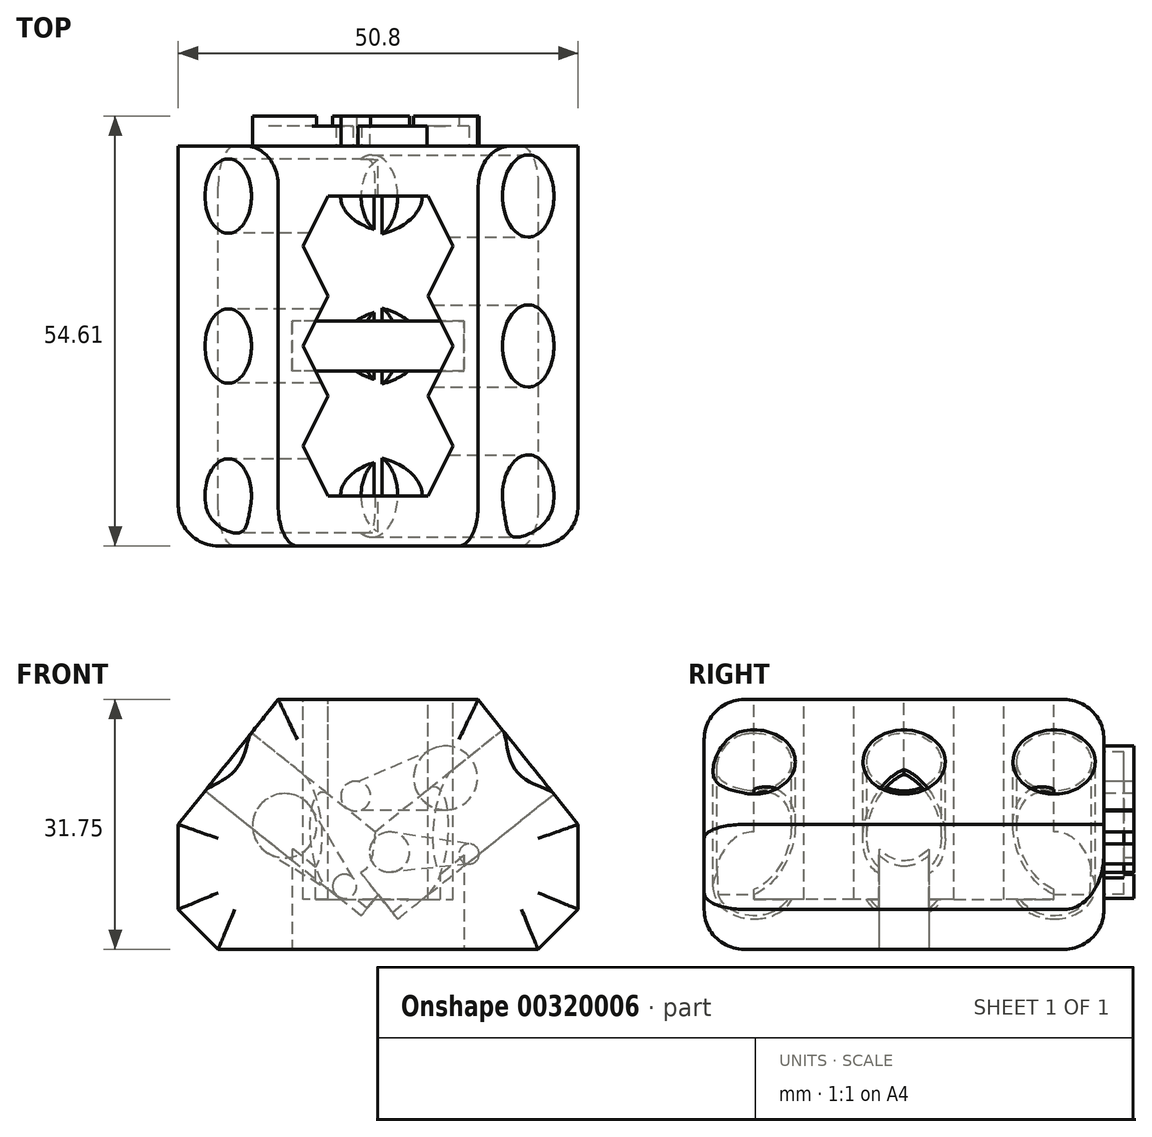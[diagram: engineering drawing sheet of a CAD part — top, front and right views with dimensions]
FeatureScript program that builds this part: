
annotation { "Feature Type Name" : "Feature", "Feature Type Description" : "" }
export const myFeature = defineFeature(function(context is Context, id is Id, definition is map)
    precondition{}
    {
        {
            var Q0;
            Q0=qCreatedBy(makeId("Top.planeOp"),FACE);
            var sketch = newSketch(context, id + "F0", { "sketchPlane" : qUnion([Q0])});
            skLineSegment(sketch, "E0.bottom", {"start": v(-25.4, 30.27) * mm, "end": v(25.4, 30.27) * mm});
            skLineSegment(sketch, "E0.top", {"start": v(-25.4, -20.53) * mm, "end": v(25.4, -20.53) * mm});
            skLineSegment(sketch, "E0.left", {"start": v(-25.4, 30.27) * mm, "end": v(-25.4, -20.53) * mm});
            skLineSegment(sketch, "E0.right", {"start": v(25.4, 30.27) * mm, "end": v(25.4, -20.53) * mm});
            skSolve(sketch);
        }
        {
            var Q0;
            Q0=makeQuery(id+"F0.imprint","IMPRINT",FACE,{"disambiguationData":[TD([[makeQuery(id+"F0.imprint","IMPRINT",EDGE,{"derivedFrom":sQuery(id+"F0.wireOp",EDGE,"E0.bottom")}),-1.0]])]});
            extrude(context, id + "F1", {"entities" : qUnion([Q0]), "depth" : 31.75 * mm});
        }
        {
            var Q0;
            Q0=makeQuery(id+"F1.opExtrude","SWEPT_FACE",FACE,{"disambiguationData":[OSD([sQuery(id+"F0.wireOp",EDGE,"E0.top")])]});
            var sketch = newSketch(context, id + "F2", { "sketchPlane" : qUnion([Q0])});
            skLineSegment(sketch, "E1", {"start": v(0, 31.75) * mm, "end": v(0, 0) * mm, "construction": true});
            skLineSegment(sketch, "E2", {"start": v(0, 0) * mm, "end": v(-25.4, 15.88) * mm, "construction": true});
            skLineSegment(sketch, "E3", {"start": v(-25.4, 15.88) * mm, "end": v(0, 31.75) * mm, "construction": true});
            skLineSegment(sketch, "E4", {"start": v(0, 0) * mm, "end": v(25.4, 15.88) * mm, "construction": true});
            skLineSegment(sketch, "E5", {"start": v(25.4, 15.87) * mm, "end": v(0, 31.75) * mm, "construction": true});
            skLineSegment(sketch, "E6", {"start": v(-12.7, 23.81) * mm, "end": v(-12.7, 31.75) * mm, "construction": true});
            skPoint(sketch, "E6.endSnap0", {"position": v(-12.7, 23.81) * mm});
            skLineSegment(sketch, "E7", {"start": v(12.7, 23.81) * mm, "end": v(12.7, 31.75) * mm, "construction": true});
            skPoint(sketch, "E7.endSnap0", {"position": v(12.7, 23.81) * mm});
            skLineSegment(sketch, "E8", {"start": v(-12.7, 31.75) * mm, "end": v(-25.4, 15.88) * mm});
            skLineSegment(sketch, "E9", {"start": v(12.7, 31.75) * mm, "end": v(25.4, 15.87) * mm});
            skSolve(sketch);
        }
        {
            var Q0;
            {var subQ0=sQuery(id+"F2.wireOp",EDGE,"E8");Q0=makeQuery(id+"F2.imprint","IMPRINT",FACE,{"disambiguationData":[TD([[makeQuery(id+"F2.imprint","IMPRINT",EDGE,{"derivedFrom":subQ0}),-1.0]])]});}
            var Q1;
            {var subQ0=sQuery(id+"F2.wireOp",EDGE,"E9");Q1=makeQuery(id+"F2.imprint","IMPRINT",FACE,{"disambiguationData":[TD([[makeQuery(id+"F2.imprint","IMPRINT",EDGE,{"derivedFrom":subQ0}),1.0]])]});}
            extrude(context, id + "F3", {"entities" : qUnion([Q0, Q1]), "operationType" : NewBodyOperationType.REMOVE, "oppositeDirection" : true, "depth" : 50.8 * mm});
        }
        {
            var Q0;
            Q0=makeQuery(id+"F3.boolean.opBoolean","COPY",FACE,{"derivedFrom":makeQuery(id+"F3.opExtrude","SWEPT_FACE",FACE,{"disambiguationData":[OSD([sQuery(id+"F2.wireOp",EDGE,"E8")])]})});
            var sketch = newSketch(context, id + "F4", { "sketchPlane" : qUnion([Q0])});
            skLineSegment(sketch, "E10", {"start": v(-30.27, 16.86) * mm, "end": v(-4.87, 16.86) * mm, "construction": true});
            skLineSegment(sketch, "E11", {"start": v(-4.87, 16.86) * mm, "end": v(-4.87, -3.47) * mm, "construction": true});
            skLineSegment(sketch, "E12", {"start": v(-4.87, 6.7) * mm, "end": v(20.53, 6.7) * mm, "construction": true});
            skLineSegment(sketch, "E13", {"start": v(20.53, 6.7) * mm, "end": v(7.83, 6.7) * mm, "construction": true});
            skLineSegment(sketch, "E14", {"start": v(-30.27, 6.7) * mm, "end": v(-4.87, 6.7) * mm, "construction": true});
            skLineSegment(sketch, "E15", {"start": v(-17.57, 6.7) * mm, "end": v(-4.87, 6.7) * mm, "construction": true});
            skLineSegment(sketch, "E16", {"start": v(-17.57, 6.7) * mm, "end": v(-17.57, 16.86) * mm, "construction": true});
            skLineSegment(sketch, "E17", {"start": v(-17.57, 16.86) * mm, "end": v(7.83, 16.86) * mm, "construction": true});
            skLineSegment(sketch, "E18", {"start": v(7.83, 16.86) * mm, "end": v(7.83, 6.7) * mm, "construction": true});
            skLineSegment(sketch, "E19", {"start": v(14.18, 6.7) * mm, "end": v(7.83, 6.7) * mm, "construction": true});
            skLineSegment(sketch, "E20", {"start": v(-30.27, 6.7) * mm, "end": v(-17.57, 6.7) * mm, "construction": true});
            skLineSegment(sketch, "E21", {"start": v(-17.57, -3.47) * mm, "end": v(-17.57, 6.7) * mm, "construction": true});
            skLineSegment(sketch, "E22", {"start": v(-23.92, 6.7) * mm, "end": v(-17.57, 6.7) * mm, "construction": true});
            skCircle(sketch, "E23", {"center": v(-23.92, 6.7) * mm, "radius": 4.72 * mm});
            skLineSegment(sketch, "E24", {"start": v(-23.92, 11.42) * mm, "end": v(20.53, 11.42) * mm, "construction": true});
            skLineSegment(sketch, "E25", {"start": v(-4.87, 11.42) * mm, "end": v(7.83, 11.42) * mm, "construction": true});
            skLineSegment(sketch, "E26", {"start": v(7.83, 11.42) * mm, "end": v(14.18, 11.42) * mm, "construction": true});
            skCircle(sketch, "E27", {"center": v(-4.87, 6.7) * mm, "radius": 4.72 * mm});
            skCircle(sketch, "E28", {"center": v(14.18, 6.7) * mm, "radius": 4.72 * mm});
            skSolve(sketch);
        }
        {
            var Q0;
            Q0 = qSketchRegion(id + "F4", true);
            extrude(context, id + "F5", {"entities" : qUnion([Q0]), "operationType" : NewBodyOperationType.REMOVE, "oppositeDirection" : true, "depth" : 25.4 * mm});
        }
        {
            var Q0;
            Q0=makeQuery(id+"F3.boolean.opBoolean","COPY",FACE,{"derivedFrom":makeQuery(id+"F3.opExtrude","SWEPT_FACE",FACE,{"disambiguationData":[OSD([sQuery(id+"F2.wireOp",EDGE,"E9")])]})});
            var sketch = newSketch(context, id + "F6", { "sketchPlane" : qUnion([Q0])});
            skLineSegment(sketch, "E29", {"start": v(-20.53, 16.86) * mm, "end": v(4.87, 16.86) * mm, "construction": true});
            skLineSegment(sketch, "E30", {"start": v(4.87, 16.86) * mm, "end": v(4.87, -3.47) * mm, "construction": true});
            skLineSegment(sketch, "E31", {"start": v(4.87, -3.47) * mm, "end": v(30.27, -3.47) * mm, "construction": true});
            skLineSegment(sketch, "E32", {"start": v(30.27, -3.47) * mm, "end": v(30.27, 16.86) * mm, "construction": true});
            skLineSegment(sketch, "E33", {"start": v(30.27, 16.86) * mm, "end": v(4.87, 16.86) * mm, "construction": true});
            skLineSegment(sketch, "E34", {"start": v(4.87, 6.7) * mm, "end": v(30.27, 6.7) * mm, "construction": true});
            skLineSegment(sketch, "E35", {"start": v(30.27, 6.7) * mm, "end": v(17.57, 6.7) * mm, "construction": true});
            skLineSegment(sketch, "E36", {"start": v(17.57, 6.7) * mm, "end": v(23.92, 6.7) * mm, "construction": true});
            skLineSegment(sketch, "E37", {"start": v(-20.53, 6.7) * mm, "end": v(4.87, 6.7) * mm, "construction": true});
            skLineSegment(sketch, "E38", {"start": v(-7.83, 6.7) * mm, "end": v(4.87, 6.7) * mm, "construction": true});
            skLineSegment(sketch, "E39", {"start": v(-20.53, -3.47) * mm, "end": v(4.87, -3.47) * mm, "construction": true});
            skLineSegment(sketch, "E40", {"start": v(-20.53, -3.47) * mm, "end": v(-20.53, 16.86) * mm, "construction": true});
            skLineSegment(sketch, "E41", {"start": v(-20.53, 6.7) * mm, "end": v(-7.83, 6.7) * mm, "construction": true});
            skLineSegment(sketch, "E42", {"start": v(-14.18, 6.7) * mm, "end": v(-7.83, 6.7) * mm, "construction": true});
            skLineSegment(sketch, "E43", {"start": v(4.87, 11.92) * mm, "end": v(30.27, 11.92) * mm, "construction": true});
            skLineSegment(sketch, "E44", {"start": v(30.27, 11.92) * mm, "end": v(23.92, 11.92) * mm, "construction": true});
            skLineSegment(sketch, "E45", {"start": v(23.92, 11.92) * mm, "end": v(-14.18, 11.92) * mm, "construction": true});
            skCircle(sketch, "E46", {"center": v(-14.18, 6.7) * mm, "radius": 5.23 * mm});
            skCircle(sketch, "E47", {"center": v(4.87, 6.7) * mm, "radius": 5.23 * mm});
            skCircle(sketch, "E48", {"center": v(23.92, 6.7) * mm, "radius": 5.23 * mm});
            skSolve(sketch);
        }
        {
            var Q0;
            Q0=makeQuery(id+"F6.imprint","IMPRINT",FACE,{"disambiguationData":[TD([[makeQuery(id+"F6.imprint","IMPRINT",EDGE,{"derivedFrom":sQuery(id+"F6.wireOp",EDGE,"E46")}),1.0]])]});
            var Q1;
            Q1=makeQuery(id+"F6.imprint","IMPRINT",FACE,{"disambiguationData":[TD([[makeQuery(id+"F6.imprint","IMPRINT",EDGE,{"derivedFrom":sQuery(id+"F6.wireOp",EDGE,"E47")}),1.0]])]});
            var Q2;
            Q2=makeQuery(id+"F6.imprint","IMPRINT",FACE,{"disambiguationData":[TD([[makeQuery(id+"F6.imprint","IMPRINT",EDGE,{"derivedFrom":sQuery(id+"F6.wireOp",EDGE,"E48")}),1.0]])]});
            extrude(context, id + "F7", {"entities" : qUnion([Q0, Q1, Q2]), "operationType" : NewBodyOperationType.REMOVE, "oppositeDirection" : true, "depth" : 25.4 * mm});
        }
        {
            var Q0;
            Q0=makeQuery(id+"F3.boolean.opBoolean","COPY",EDGE,{"derivedFrom":makeQuery(id+"F3.opExtrude","SWEPT_EDGE",EDGE,{"disambiguationData":[OSD([sQuery(id+"F0.wireOp",EDGE,"E0.top"),sQuery(id+"F0.wireOp",EDGE,"E0.right"),sQuery(id+"F2.wireOp",EDGE,"E9")])]})});
            var Q1;
            Q1=makeQuery(id+"F3.boolean.opBoolean","COPY",EDGE,{"derivedFrom":makeQuery(id+"F3.opExtrude","SWEPT_EDGE",EDGE,{"disambiguationData":[OSD([sQuery(id+"F0.wireOp",EDGE,"E0.top"),sQuery(id+"F0.wireOp",EDGE,"E0.left"),sQuery(id+"F2.wireOp",EDGE,"E8")])]})});
            var Q2;
            Q2=makeQuery(id+"F1.opExtrude","CAP_EDGE",EDGE,{"disambiguationData":[OSD([sQuery(id+"F0.wireOp",EDGE,"E0.left")])],"isStart":true});
            var Q3;
            Q3=makeQuery(id+"F1.opExtrude","CAP_EDGE",EDGE,{"disambiguationData":[OSD([sQuery(id+"F0.wireOp",EDGE,"E0.right")])],"isStart":true});
            chamfer(context, id + "F8", {"entities" : qUnion([Q0, Q1, Q2, Q3]), "width" : 5.08 * mm, "tangentPropagation" : true});
        }
        {
            var Q0;
            Q0=makeQuery(id+"F1.opExtrude","CAP_FACE",FACE,{"disambiguationData":[OSD([sQuery(id+"F0.wireOp",EDGE,"E0.bottom"),sQuery(id+"F0.wireOp",EDGE,"E0.top"),sQuery(id+"F0.wireOp",EDGE,"E0.left"),sQuery(id+"F0.wireOp",EDGE,"E0.right")])],"isStart":false});
            var sketch = newSketch(context, id + "F9", { "sketchPlane" : qUnion([Q0])});
            skLineSegment(sketch, "E49", {"start": v(0, 30.27) * mm, "end": v(0, -20.53) * mm, "construction": true});
            skLineSegment(sketch, "E50", {"start": v(0, -20.53) * mm, "end": v(0, 4.87) * mm, "construction": true});
            skLineSegment(sketch, "E51", {"start": v(0, 4.87) * mm, "end": v(12.7, 4.87) * mm, "construction": true});
            skLineSegment(sketch, "E52", {"start": v(12.7, 4.87) * mm, "end": v(-12.7, 4.87) * mm, "construction": true});
            skLineSegment(sketch, "E53", {"start": v(-12.7, 4.87) * mm, "end": v(-12.7, 30.27) * mm, "construction": true});
            skLineSegment(sketch, "E54", {"start": v(-12.7, 30.27) * mm, "end": v(12.7, 30.27) * mm, "construction": true});
            skLineSegment(sketch, "E55", {"start": v(12.7, 30.27) * mm, "end": v(12.7, -20.53) * mm, "construction": true});
            skLineSegment(sketch, "E56", {"start": v(12.7, -20.53) * mm, "end": v(-12.7, -20.53) * mm, "construction": true});
            skLineSegment(sketch, "E57", {"start": v(-12.7, -20.53) * mm, "end": v(-12.7, 4.87) * mm, "construction": true});
            skLineSegment(sketch, "E58", {"start": v(-12.7, -7.83) * mm, "end": v(12.7, -7.83) * mm, "construction": true});
            skLineSegment(sketch, "E59", {"start": v(-12.7, 17.57) * mm, "end": v(12.7, 17.57) * mm, "construction": true});
            skLineSegment(sketch, "E60", {"start": v(12.7, 17.57) * mm, "end": v(0, 17.57) * mm, "construction": true});
            skLineSegment(sketch, "E61", {"start": v(-12.7, 30.27) * mm, "end": v(0, 17.57) * mm, "construction": true});
            skLineSegment(sketch, "E62", {"start": v(12.7, 30.27) * mm, "end": v(0, 17.57) * mm, "construction": true});
            skLineSegment(sketch, "E63", {"start": v(0, 17.57) * mm, "end": v(-12.7, 4.87) * mm, "construction": true});
            skLineSegment(sketch, "E64", {"start": v(12.7, 4.87) * mm, "end": v(0, 17.57) * mm, "construction": true});
            skLineSegment(sketch, "E65", {"start": v(-12.7, 4.87) * mm, "end": v(0, -7.83) * mm, "construction": true});
            skLineSegment(sketch, "E66", {"start": v(0, -7.83) * mm, "end": v(12.7, 4.87) * mm, "construction": true});
            skLineSegment(sketch, "E67", {"start": v(0, -7.83) * mm, "end": v(-12.7, -20.53) * mm, "construction": true});
            skLineSegment(sketch, "E68", {"start": v(0, -7.83) * mm, "end": v(12.7, -20.53) * mm, "construction": true});
            skLineSegment(sketch, "E69", {"start": v(-6.35, 23.92) * mm, "end": v(6.35, 23.92) * mm, "construction": true});
            skLineSegment(sketch, "E70", {"start": v(-6.35, 11.22) * mm, "end": v(6.35, 11.22) * mm, "construction": true});
            skLineSegment(sketch, "E71", {"start": v(-6.35, -1.48) * mm, "end": v(6.35, -1.48) * mm, "construction": true});
            skLineSegment(sketch, "E72", {"start": v(-6.35, -14.18) * mm, "end": v(6.35, -14.18) * mm, "construction": true});
            skLineSegment(sketch, "E73", {"start": v(-12.7, 17.57) * mm, "end": v(0, 17.57) * mm, "construction": true});
            skLineSegment(sketch, "E74", {"start": v(-6.35, 23.92) * mm, "end": v(-6.35, 17.57) * mm, "construction": true});
            skLineSegment(sketch, "E75", {"start": v(-6.35, 17.57) * mm, "end": v(6.35, 17.57) * mm, "construction": true});
            skLineSegment(sketch, "E76", {"start": v(6.35, 17.57) * mm, "end": v(6.35, 23.92) * mm, "construction": true});
            skLineSegment(sketch, "E77", {"start": v(-12.7, 17.57) * mm, "end": v(-6.35, 17.57) * mm, "construction": true});
            skLineSegment(sketch, "E78", {"start": v(-9.53, 20.75) * mm, "end": v(-9.53, 17.57) * mm, "construction": true});
            skPoint(sketch, "E78.startSnap0", {"position": v(-6.35, 20.75) * mm});
            skPoint(sketch, "E78.startSnap1", {"position": v(-9.53, 17.57) * mm});
            skLineSegment(sketch, "E79", {"start": v(-9.53, 17.57) * mm, "end": v(6.35, 17.57) * mm, "construction": true});
            skLineSegment(sketch, "E80", {"start": v(-9.53, 17.57) * mm, "end": v(-9.53, -20.53) * mm, "construction": true});
            skLineSegment(sketch, "E81", {"start": v(12.7, 17.57) * mm, "end": v(6.35, 23.92) * mm, "construction": true});
            skLineSegment(sketch, "E82", {"start": v(6.35, 17.57) * mm, "end": v(12.7, 23.92) * mm, "construction": true});
            skLineSegment(sketch, "E83", {"start": v(12.7, 23.92) * mm, "end": v(9.52, 20.75) * mm, "construction": true});
            skLineSegment(sketch, "E84", {"start": v(9.52, 20.75) * mm, "end": v(9.52, 17.57) * mm, "construction": true});
            skLineSegment(sketch, "E85", {"start": v(9.52, 17.57) * mm, "end": v(9.52, -20.53) * mm, "construction": true});
            skLineSegment(sketch, "E86", {"start": v(-6.35, 23.92) * mm, "end": v(-9.53, 17.57) * mm});
            skLineSegment(sketch, "E87", {"start": v(-9.53, 17.57) * mm, "end": v(-6.35, 11.22) * mm});
            skLineSegment(sketch, "E88", {"start": v(-6.35, 11.22) * mm, "end": v(-9.53, 4.87) * mm});
            skLineSegment(sketch, "E89", {"start": v(-9.53, 4.87) * mm, "end": v(-6.35, -1.48) * mm});
            skLineSegment(sketch, "E90", {"start": v(-6.35, -1.48) * mm, "end": v(-9.53, -7.83) * mm});
            skLineSegment(sketch, "E91", {"start": v(-9.53, -7.83) * mm, "end": v(-6.35, -14.18) * mm});
            skLineSegment(sketch, "E92", {"start": v(6.35, -14.18) * mm, "end": v(-6.35, -14.18) * mm});
            skLineSegment(sketch, "E93", {"start": v(9.52, -7.83) * mm, "end": v(6.35, -14.18) * mm});
            skLineSegment(sketch, "E94", {"start": v(6.35, -1.48) * mm, "end": v(9.52, -7.83) * mm});
            skLineSegment(sketch, "E95", {"start": v(9.52, 4.87) * mm, "end": v(6.35, -1.48) * mm});
            skLineSegment(sketch, "E96", {"start": v(6.35, 11.22) * mm, "end": v(9.52, 4.87) * mm});
            skLineSegment(sketch, "E97", {"start": v(6.35, 11.22) * mm, "end": v(9.52, 17.57) * mm});
            skLineSegment(sketch, "E98", {"start": v(6.35, 23.92) * mm, "end": v(9.52, 17.57) * mm});
            skLineSegment(sketch, "E99", {"start": v(-6.35, 23.92) * mm, "end": v(6.35, 23.92) * mm});
            skSolve(sketch);
        }
        {
            var Q0;
            Q0=makeQuery(id+"F9.imprint","IMPRINT",FACE,{"disambiguationData":[TD([[makeQuery(id+"F9.imprint","IMPRINT",EDGE,{"derivedFrom":sQuery(id+"F9.wireOp",EDGE,"E86")}),1.0]])]});
            extrude(context, id + "F10", {"entities" : qUnion([Q0]), "operationType" : NewBodyOperationType.REMOVE, "oppositeDirection" : true, "depth" : 25.4 * mm});
        }
        {
            var Q0;
            Q0=makeQuery(id+"F1.opExtrude","CAP_FACE",FACE,{"disambiguationData":[OSD([sQuery(id+"F0.wireOp",EDGE,"E0.bottom"),sQuery(id+"F0.wireOp",EDGE,"E0.top"),sQuery(id+"F0.wireOp",EDGE,"E0.left"),sQuery(id+"F0.wireOp",EDGE,"E0.right")])],"isStart":true});
            var sketch = newSketch(context, id + "F11", { "sketchPlane" : qUnion([Q0])});
            skLineSegment(sketch, "E100", {"start": v(-10.92, -4.87) * mm, "end": v(10.92, -4.87) * mm, "construction": true});
            skLineSegment(sketch, "E101", {"start": v(10.92, -4.87) * mm, "end": v(10.92, -30.27) * mm, "construction": true});
            skLineSegment(sketch, "E102", {"start": v(10.92, -30.27) * mm, "end": v(-10.92, -30.27) * mm, "construction": true});
            skLineSegment(sketch, "E103", {"start": v(-10.92, -30.27) * mm, "end": v(-10.92, -4.87) * mm, "construction": true});
            skLineSegment(sketch, "E104", {"start": v(10.92, -17.57) * mm, "end": v(-10.92, -17.57) * mm, "construction": true});
            skLineSegment(sketch, "E105", {"start": v(-10.92, -4.87) * mm, "end": v(-10.92, 20.53) * mm, "construction": true});
            skLineSegment(sketch, "E106", {"start": v(-10.92, 20.53) * mm, "end": v(10.92, 20.53) * mm, "construction": true});
            skLineSegment(sketch, "E107", {"start": v(10.92, 20.53) * mm, "end": v(10.92, -4.87) * mm, "construction": true});
            skLineSegment(sketch, "E108", {"start": v(10.92, 7.83) * mm, "end": v(-10.92, 7.83) * mm, "construction": true});
            skLineSegment(sketch, "E109", {"start": v(-10.92, 7.83) * mm, "end": v(-10.92, -4.87) * mm, "construction": true});
            skLineSegment(sketch, "E110", {"start": v(-10.92, 1.48) * mm, "end": v(10.92, 1.48) * mm, "construction": true});
            skLineSegment(sketch, "E111", {"start": v(-10.92, -4.87) * mm, "end": v(-10.92, -17.57) * mm, "construction": true});
            skLineSegment(sketch, "E112", {"start": v(-10.92, -11.22) * mm, "end": v(10.92, -11.22) * mm, "construction": true});
            skLineSegment(sketch, "E113", {"start": v(10.92, 1.48) * mm, "end": v(10.92, -4.87) * mm, "construction": true});
            skLineSegment(sketch, "E114", {"start": v(10.92, -1.7) * mm, "end": v(-10.92, -1.7) * mm, "construction": true});
            skLineSegment(sketch, "E115", {"start": v(-10.92, -1.7) * mm, "end": v(-10.92, -11.22) * mm, "construction": true});
            skLineSegment(sketch, "E116", {"start": v(10.92, -4.87) * mm, "end": v(10.92, -11.22) * mm, "construction": true});
            skLineSegment(sketch, "E117", {"start": v(10.92, -8.05) * mm, "end": v(-10.92, -8.05) * mm, "construction": true});
            skLineSegment(sketch, "E118", {"start": v(10.92, -1.7) * mm, "end": v(-10.92, -1.7) * mm});
            skLineSegment(sketch, "E119", {"start": v(-10.92, -1.7) * mm, "end": v(-10.92, -8.05) * mm});
            skLineSegment(sketch, "E120", {"start": v(10.92, -8.05) * mm, "end": v(-10.92, -8.05) * mm});
            skLineSegment(sketch, "E121", {"start": v(10.92, -8.05) * mm, "end": v(10.92, -1.7) * mm});
            skSolve(sketch);
        }
        {
            var Q0;
            Q0=makeQuery(id+"F11.imprint","IMPRINT",FACE,{"disambiguationData":[TD([[makeQuery(id+"F11.imprint","IMPRINT",EDGE,{"derivedFrom":sQuery(id+"F11.wireOp",EDGE,"E118")}),1.0]])]});
            extrude(context, id + "F12", {"entities" : qUnion([Q0]), "operationType" : NewBodyOperationType.REMOVE, "oppositeDirection" : true, "depth" : 12.7 * mm});
        }
        {
            var Q0;
            Q0=makeQuery(id+"F1.opExtrude","CAP_EDGE",EDGE,{"disambiguationData":[OSD([sQuery(id+"F0.wireOp",EDGE,"E0.top")])],"isStart":false});
            var Q1;
            Q1=makeQuery(id+"F1.opExtrude","SWEPT_FACE",FACE,{"disambiguationData":[OSD([sQuery(id+"F0.wireOp",EDGE,"E0.top")])]});
            var Q2;
            Q2=makeQuery(id+"F1.opExtrude","CAP_EDGE",EDGE,{"disambiguationData":[OSD([sQuery(id+"F0.wireOp",EDGE,"E0.bottom")])],"isStart":false});
            var Q3;
            Q3=makeQuery(id+"F3.boolean.opBoolean","COPY",EDGE,{"derivedFrom":makeQuery(id+"F3.opExtrude","CAP_EDGE",EDGE,{"disambiguationData":[OSD([sQuery(id+"F2.wireOp",EDGE,"E9")])],"isStart":false})});
            var Q4;
            Q4=makeQuery(id+"F8.opChamfer","BLEND_EDGE",EDGE,{"blendedFrom":[makeQuery(id+"F1.opExtrude","CAP_EDGE",EDGE,{"disambiguationData":[OSD([sQuery(id+"F0.wireOp",EDGE,"E0.right")])],"isStart":true}),makeQuery(id+"F1.opExtrude","SWEPT_FACE",FACE,{"disambiguationData":[OSD([sQuery(id+"F0.wireOp",EDGE,"E0.bottom")])]})],"blendedInto":[makeQuery(id+"F1.opExtrude","SWEPT_FACE",FACE,{"disambiguationData":[OSD([sQuery(id+"F0.wireOp",EDGE,"E0.bottom")])]})]});
            var Q5;
            Q5=makeQuery(id+"F1.opExtrude","CAP_EDGE",EDGE,{"disambiguationData":[OSD([sQuery(id+"F0.wireOp",EDGE,"E0.bottom")])],"isStart":true});
            var Q6;
            Q6=makeQuery(id+"F8.opChamfer","BLEND_EDGE",EDGE,{"blendedFrom":[makeQuery(id+"F1.opExtrude","CAP_EDGE",EDGE,{"disambiguationData":[OSD([sQuery(id+"F0.wireOp",EDGE,"E0.left")])],"isStart":true}),makeQuery(id+"F1.opExtrude","SWEPT_FACE",FACE,{"disambiguationData":[OSD([sQuery(id+"F0.wireOp",EDGE,"E0.bottom")])]})],"blendedInto":[makeQuery(id+"F1.opExtrude","SWEPT_FACE",FACE,{"disambiguationData":[OSD([sQuery(id+"F0.wireOp",EDGE,"E0.bottom")])]})]});
            var Q7;
            Q7=makeQuery(id+"F8.opChamfer","BLEND_EDGE",EDGE,{"blendedFrom":[makeQuery(id+"F3.boolean.opBoolean","COPY",EDGE,{"derivedFrom":makeQuery(id+"F3.opExtrude","SWEPT_EDGE",EDGE,{"disambiguationData":[OSD([sQuery(id+"F0.wireOp",EDGE,"E0.top"),sQuery(id+"F0.wireOp",EDGE,"E0.left"),sQuery(id+"F2.wireOp",EDGE,"E8")])]})}),makeQuery(id+"F1.opExtrude","SWEPT_FACE",FACE,{"disambiguationData":[OSD([sQuery(id+"F0.wireOp",EDGE,"E0.bottom")])]})],"blendedInto":[makeQuery(id+"F1.opExtrude","SWEPT_FACE",FACE,{"disambiguationData":[OSD([sQuery(id+"F0.wireOp",EDGE,"E0.bottom")])]})]});
            var Q8;
            Q8=makeQuery(id+"F3.boolean.opBoolean","COPY",EDGE,{"derivedFrom":makeQuery(id+"F3.opExtrude","CAP_EDGE",EDGE,{"disambiguationData":[OSD([sQuery(id+"F2.wireOp",EDGE,"E8")])],"isStart":false})});
            var Q9;
            {var subQ0=sQuery(id+"F0.wireOp",EDGE,"E0.right");Q9=makeQuery(id+"F8.opChamfer","BLEND_EDGE",EDGE,{"blendedFrom":[makeQuery(id+"F1.opExtrude","CAP_EDGE",EDGE,{"disambiguationData":[OSD([subQ0])],"isStart":true}),makeQuery(id+"F3.boolean.opBoolean","COPY",EDGE,{"derivedFrom":makeQuery(id+"F3.opExtrude","SWEPT_EDGE",EDGE,{"disambiguationData":[OSD([sQuery(id+"F0.wireOp",EDGE,"E0.top"),subQ0,sQuery(id+"F2.wireOp",EDGE,"E9")])]})})],"blendedInto":[]});}
            var Q10;
            {var subQ0=sQuery(id+"F0.wireOp",EDGE,"E0.left");Q10=makeQuery(id+"F8.opChamfer","BLEND_EDGE",EDGE,{"blendedFrom":[makeQuery(id+"F1.opExtrude","CAP_EDGE",EDGE,{"disambiguationData":[OSD([subQ0])],"isStart":true}),makeQuery(id+"F3.boolean.opBoolean","COPY",EDGE,{"derivedFrom":makeQuery(id+"F3.opExtrude","SWEPT_EDGE",EDGE,{"disambiguationData":[OSD([sQuery(id+"F0.wireOp",EDGE,"E0.top"),subQ0,sQuery(id+"F2.wireOp",EDGE,"E8")])]})})],"blendedInto":[]});}
            var Q11;
            Q11=makeQuery(id+"F3.boolean.opBoolean","COPY",EDGE,{"derivedFrom":makeQuery(id+"F3.opExtrude","SWEPT_EDGE",EDGE,{"disambiguationData":[OSD([sQuery(id+"F0.wireOp",EDGE,"E0.top"),sQuery(id+"F2.wireOp",EDGE,"E8")])]})});
            var Q12;
            Q12=makeQuery(id+"F3.boolean.opBoolean","COPY",EDGE,{"derivedFrom":makeQuery(id+"F3.opExtrude","SWEPT_EDGE",EDGE,{"disambiguationData":[OSD([sQuery(id+"F0.wireOp",EDGE,"E0.top"),sQuery(id+"F2.wireOp",EDGE,"E9")])]})});
            fillet(context, id + "F13", {"entities" : qUnion([Q0, Q1, Q2, Q3, Q4, Q5, Q6, Q7, Q8, Q9, Q10, Q11, Q12]), "radius" : 5.08 * mm, "tangentPropagation" : true, "allowEdgeOverflow" : false});
        }
        {
            var Q0;
            Q0=makeQuery(id+"F1.opExtrude","SWEPT_FACE",FACE,{"disambiguationData":[OSD([sQuery(id+"F0.wireOp",EDGE,"E0.bottom")])]});
            var sketch = newSketch(context, id + "F14", { "sketchPlane" : qUnion([Q0])});
            skCircle(sketch, "E122", {"center": v(-8.56, 21.78) * mm, "radius": 4.05 * mm});
            skCircle(sketch, "E123", {"center": v(2.85, 19.48) * mm, "radius": 1.9 * mm});
            skCircle(sketch, "E124", {"center": v(11.88, 15.71) * mm, "radius": 4.08 * mm});
            skCircle(sketch, "E125", {"center": v(4.26, 8.01) * mm, "radius": 1.52 * mm});
            skCircle(sketch, "E126", {"center": v(-1.45, 12.36) * mm, "radius": 2.55 * mm});
            skCircle(sketch, "E127", {"center": v(-11.55, 12.12) * mm, "radius": 1.28 * mm});
            skLineSegment(sketch, "E128", {"start": v(-11.55, 13.4) * mm, "end": v(-1.83, 14.88) * mm});
            skLineSegment(sketch, "E129", {"start": v(-11.55, 10.85) * mm, "end": v(-1.71, 9.83) * mm});
            skLineSegment(sketch, "E130", {"start": v(3.19, 9.09) * mm, "end": v(8.37, 17.8) * mm});
            skLineSegment(sketch, "E131", {"start": v(5.36, 6.96) * mm, "end": v(14, 12.23) * mm});
            skLineSegment(sketch, "E132", {"start": v(2.08, 17.75) * mm, "end": v(-8.55, 17.74) * mm});
            skLineSegment(sketch, "E133", {"start": v(2.58, 21.35) * mm, "end": v(-6.2, 25.08) * mm});
            skSolve(sketch);
        }
        {
            var Q0;
            {var subQ0=sQuery(id+"F14.wireOp",EDGE,"E122");var subQ1=makeQuery(id+"F14.imprint","INTERSECT",VERTEX,{"derivedFrom":[subQ0,sQuery(id+"F14.wireOp",EDGE,"MwWy7IKR-fUUW-ASPR-3WSA-CsBmiXPVFMYq")]});Q0=makeQuery(id+"F14.imprint","IMPRINT",FACE,{"disambiguationData":[TD([[makeQuery(id+"F14.imprint","IMPRINT",EDGE,{"disambiguationData":[TD([[subQ1,-1.0]])],"derivedFrom":subQ0}),1.0]])]});}
            var Q1;
            {var subQ0=sQuery(id+"F14.wireOp",EDGE,"E127");var subQ1=makeQuery(id+"F14.imprint","INTERSECT",VERTEX,{"derivedFrom":[subQ0,sQuery(id+"F14.wireOp",EDGE,"E128")]});Q1=makeQuery(id+"F14.imprint","IMPRINT",FACE,{"disambiguationData":[TD([[makeQuery(id+"F14.imprint","IMPRINT",EDGE,{"disambiguationData":[TD([[subQ1,-1.0]])],"derivedFrom":subQ0}),1.0]])]});}
            var Q2;
            {var subQ0=sQuery(id+"F14.wireOp",EDGE,"E126");var subQ1=makeQuery(id+"F14.imprint","INTERSECT",VERTEX,{"derivedFrom":[subQ0,sQuery(id+"F14.wireOp",EDGE,"E128")]});Q2=makeQuery(id+"F14.imprint","IMPRINT",FACE,{"disambiguationData":[TD([[makeQuery(id+"F14.imprint","IMPRINT",EDGE,{"disambiguationData":[TD([[subQ1,-1.0]])],"derivedFrom":subQ0}),1.0]])]});}
            var Q3;
            {var subQ0=sQuery(id+"F14.wireOp",EDGE,"E124");var subQ1=makeQuery(id+"F14.imprint","INTERSECT",VERTEX,{"derivedFrom":[subQ0,sQuery(id+"F14.wireOp",EDGE,"E130")]});Q3=makeQuery(id+"F14.imprint","IMPRINT",FACE,{"disambiguationData":[TD([[makeQuery(id+"F14.imprint","IMPRINT",EDGE,{"disambiguationData":[TD([[subQ1,-1.0]])],"derivedFrom":subQ0}),1.0]])]});}
            var Q4;
            {var subQ0=sQuery(id+"F14.wireOp",EDGE,"E125");var subQ1=makeQuery(id+"F14.imprint","INTERSECT",VERTEX,{"derivedFrom":[subQ0,sQuery(id+"F14.wireOp",EDGE,"E130")]});Q4=makeQuery(id+"F14.imprint","IMPRINT",FACE,{"disambiguationData":[TD([[makeQuery(id+"F14.imprint","IMPRINT",EDGE,{"disambiguationData":[TD([[subQ1,-1.0]])],"derivedFrom":subQ0}),1.0]])]});}
            var Q5;
            {var subQ0=sQuery(id+"F14.wireOp",EDGE,"E123");var subQ1=makeQuery(id+"F14.imprint","INTERSECT",VERTEX,{"derivedFrom":[subQ0,sQuery(id+"F14.wireOp",EDGE,"E132")]});Q5=makeQuery(id+"F14.imprint","IMPRINT",FACE,{"disambiguationData":[TD([[makeQuery(id+"F14.imprint","IMPRINT",EDGE,{"disambiguationData":[TD([[subQ1,1.0]])],"derivedFrom":subQ0}),1.0]])]});}
            extrude(context, id + "F15", {"entities" : qUnion([Q0, Q1, Q2, Q3, Q4, Q5]), "operationType" : NewBodyOperationType.ADD, "depth" : 3.8 * mm});
        }
        {
            var Q0;
            {var subQ0=sQuery(id+"F14.wireOp",EDGE,"E128");Q0=makeQuery(id+"F14.imprint","IMPRINT",FACE,{"disambiguationData":[TD([[makeQuery(id+"F14.imprint","IMPRINT",EDGE,{"derivedFrom":subQ0}),-1.0]])]});}
            var Q1;
            {var subQ0=sQuery(id+"F14.wireOp",EDGE,"E132");Q1=makeQuery(id+"F14.imprint","IMPRINT",FACE,{"disambiguationData":[TD([[makeQuery(id+"F14.imprint","IMPRINT",EDGE,{"derivedFrom":subQ0}),-1.0]])]});}
            var Q2;
            {var subQ0=sQuery(id+"F14.wireOp",EDGE,"E130");Q2=makeQuery(id+"F14.imprint","IMPRINT",FACE,{"disambiguationData":[TD([[makeQuery(id+"F14.imprint","IMPRINT",EDGE,{"derivedFrom":subQ0}),-1.0]])]});}
            extrude(context, id + "F16", {"entities" : qUnion([Q0, Q1, Q2]), "operationType" : NewBodyOperationType.ADD, "depth" : 2.54 * mm});
        }
    });
